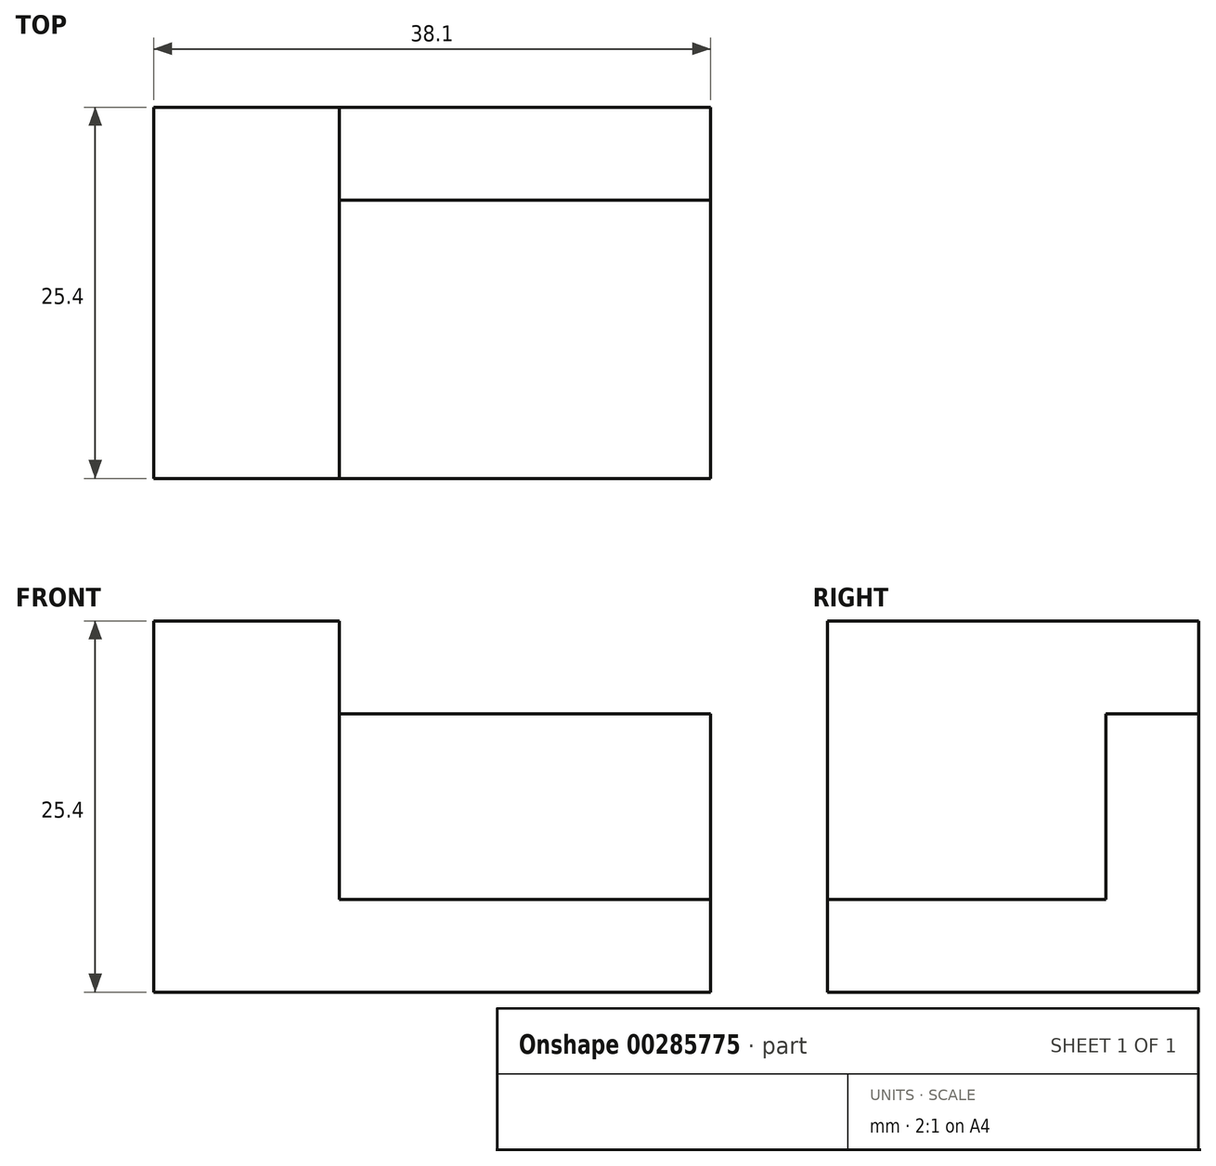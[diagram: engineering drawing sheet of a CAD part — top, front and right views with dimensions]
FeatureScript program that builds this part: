
annotation { "Feature Type Name" : "Feature", "Feature Type Description" : "" }
export const myFeature = defineFeature(function(context is Context, id is Id, definition is map)
    precondition{}
    {
        {
            var Q0;
            Q0=qCreatedBy(makeId("Right.planeOp"),FACE);
            var sketch = newSketch(context, id + "F0", { "sketchPlane" : qUnion([Q0])});
            skLineSegment(sketch, "E0", {"start": v(0, 0) * mm, "end": v(0, 25.4) * mm});
            skLineSegment(sketch, "E1", {"start": v(0, 25.4) * mm, "end": v(25.4, 25.4) * mm});
            skLineSegment(sketch, "E2", {"start": v(25.4, 25.4) * mm, "end": v(25.4, 0) * mm});
            skLineSegment(sketch, "E3", {"start": v(25.4, 0) * mm, "end": v(0, 0) * mm});
            skSolve(sketch);
        }
        {
            var Q0;
            Q0=makeQuery(id+"F0.imprint","IMPRINT",FACE,{"disambiguationData":[TD([[makeQuery(id+"F0.imprint","IMPRINT",EDGE,{"derivedFrom":sQuery(id+"F0.wireOp",EDGE,"E0")}),-1.0]])]});
            extrude(context, id + "F1", {"entities" : qUnion([Q0]), "depth" : 38.1 * mm});
        }
        {
            var Q0;
            Q0=makeQuery(id+"F1.opExtrude","CAP_FACE",FACE,{"disambiguationData":[OSD([sQuery(id+"F0.wireOp",EDGE,"E0"),sQuery(id+"F0.wireOp",EDGE,"E1"),sQuery(id+"F0.wireOp",EDGE,"E2"),sQuery(id+"F0.wireOp",EDGE,"E3")])],"isStart":false});
            var sketch = newSketch(context, id + "F2", { "sketchPlane" : qUnion([Q0])});
            skLineSegment(sketch, "E4", {"start": v(0, 0) * mm, "end": v(0, 6.35) * mm});
            skLineSegment(sketch, "E5", {"start": v(0, 6.35) * mm, "end": v(19.05, 6.35) * mm});
            skLineSegment(sketch, "E6", {"start": v(19.05, 6.35) * mm, "end": v(19.05, 19.05) * mm});
            skLineSegment(sketch, "E7", {"start": v(19.05, 19.05) * mm, "end": v(25.4, 19.05) * mm});
            skSolve(sketch);
        }
        {
            var Q0;
            {var subQ2=sQuery(id+"F2.wireOp",EDGE,"E5");Q0=makeQuery(id+"F2.imprint","IMPRINT",FACE,{"disambiguationData":[TD([[makeQuery(id+"F2.imprint","IMPRINT",EDGE,{"derivedFrom":subQ2}),1.0]])]});}
            extrude(context, id + "F3", {"entities" : qUnion([Q0]), "operationType" : NewBodyOperationType.REMOVE, "oppositeDirection" : true, "depth" : 25.4 * mm});
        }
    });
